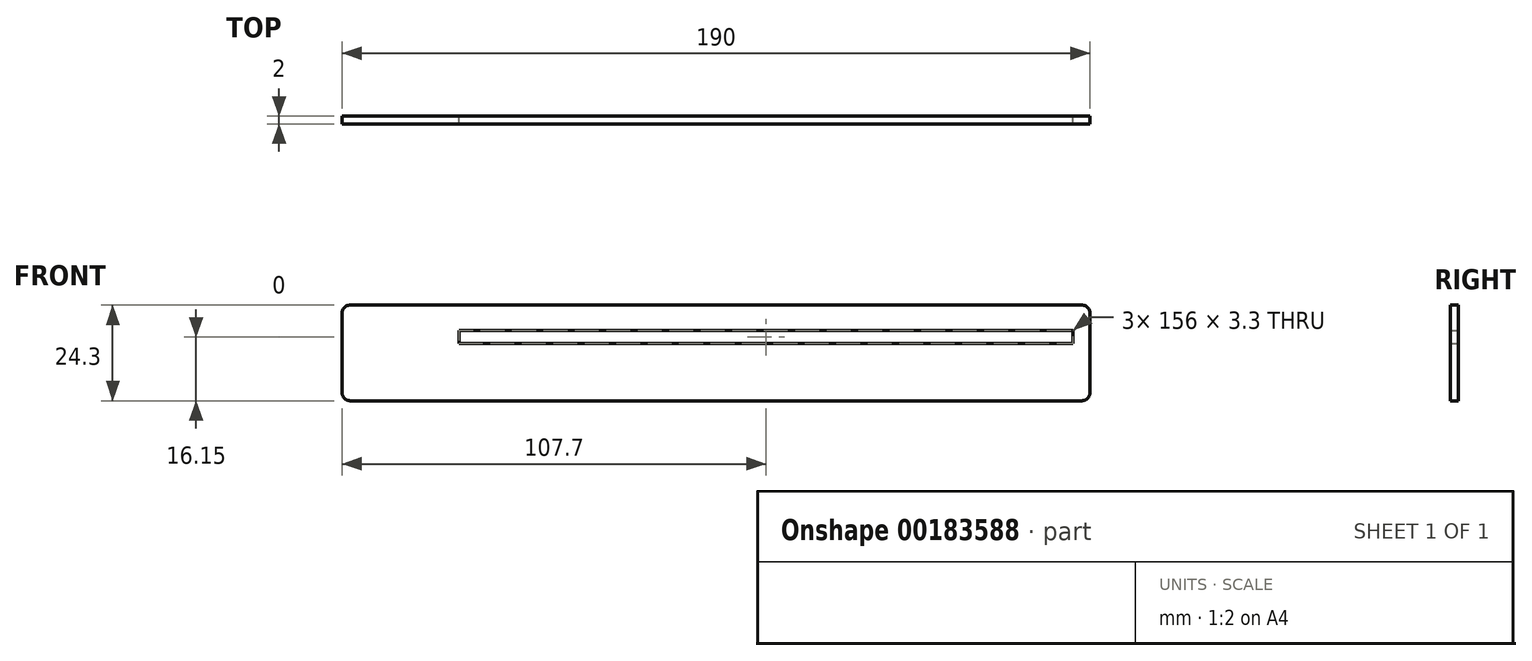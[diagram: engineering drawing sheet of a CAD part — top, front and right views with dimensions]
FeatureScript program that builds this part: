
annotation { "Feature Type Name" : "Feature", "Feature Type Description" : "" }
export const myFeature = defineFeature(function(context is Context, id is Id, definition is map)
    precondition{}
    {
        {
            var Q0;
            Q0=qCreatedBy(makeId("Front.planeOp"),FACE);
            var sketch = newSketch(context, id + "F0", { "sketchPlane" : qUnion([Q0])});
            skLineSegment(sketch, "E0.bottom", {"start": v(2, 0) * mm, "end": v(188, 0) * mm});
            skLineSegment(sketch, "E0.top", {"start": v(2, 24.3) * mm, "end": v(188, 24.3) * mm});
            skLineSegment(sketch, "E0.left", {"start": v(0, 2) * mm, "end": v(0, 22.3) * mm});
            skLineSegment(sketch, "E0.right", {"start": v(190, 2) * mm, "end": v(190, 22.3) * mm});
            skLineSegment(sketch, "E1.bottom", {"start": v(29.7, 17.8) * mm, "end": v(185.7, 17.8) * mm});
            skLineSegment(sketch, "E1.top", {"start": v(29.7, 14.5) * mm, "end": v(185.7, 14.5) * mm});
            skLineSegment(sketch, "E1.left", {"start": v(29.7, 17.8) * mm, "end": v(29.7, 14.5) * mm});
            skLineSegment(sketch, "E1.right", {"start": v(185.7, 17.8) * mm, "end": v(185.7, 14.5) * mm});
            skPoint(sketch, "E2.visualSharp", {"position": v(0, 24.3) * mm});
            skPoint(sketch, "E3.visualSharp", {"position": v(0, 0) * mm});
            skArc(sketch, "E3.filletArc", {"start": v(0, 2) * mm, "mid": v(0.59, 0.59) * mm, "end": v(2, 0) * mm});
            skPoint(sketch, "E4.visualSharp", {"position": v(190, 0) * mm});
            skArc(sketch, "E4.filletArc", {"start": v(188, 0) * mm, "mid": v(189.41, 0.59) * mm, "end": v(190, 2) * mm});
            skPoint(sketch, "E5.visualSharp", {"position": v(190, 24.3) * mm});
            skArc(sketch, "E5.filletArc", {"start": v(190, 22.3) * mm, "mid": v(189.41, 23.71) * mm, "end": v(188, 24.3) * mm});
            skArc(sketch, "E6.filletArc", {"start": v(2, 24.3) * mm, "mid": v(0.59, 23.71) * mm, "end": v(0, 22.3) * mm});
            skSolve(sketch);
        }
        {
            var Q0;
            Q0=makeQuery(id+"F0.imprint","IMPRINT",FACE,{"disambiguationData":[TD([[makeQuery(id+"F0.imprint","IMPRINT",EDGE,{"derivedFrom":sQuery(id+"F0.wireOp",EDGE,"E0.bottom")}),1.0]])]});
            extrude(context, id + "F1", {"entities" : qUnion([Q0]), "depth" : 2 * mm});
        }
    });
